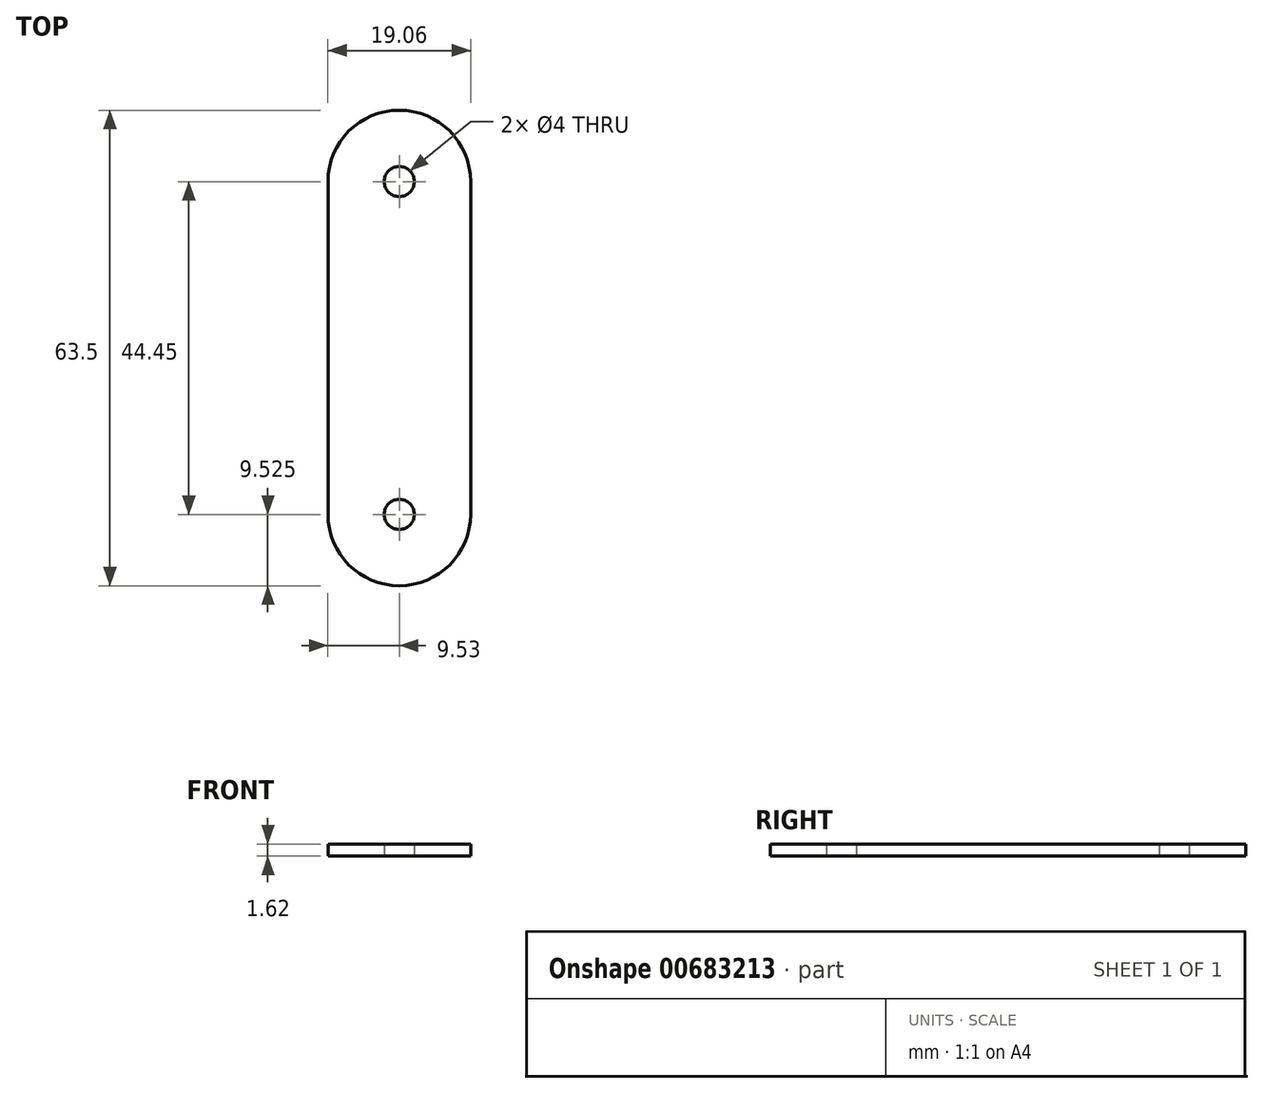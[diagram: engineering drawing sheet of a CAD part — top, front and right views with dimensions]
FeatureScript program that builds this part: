
annotation { "Feature Type Name" : "Feature", "Feature Type Description" : "" }
export const myFeature = defineFeature(function(context is Context, id is Id, definition is map)
    precondition{}
    {
        {
            var Q0;
            Q0=qCreatedBy(makeId("Top.planeOp"),FACE);
            var sketch = newSketch(context, id + "F0", { "sketchPlane" : qUnion([Q0])});
            skLineSegment(sketch, "E0.left", {"start": v(-9.52, -22.22) * mm, "end": v(-9.52, 22.23) * mm});
            skLineSegment(sketch, "E0.right", {"start": v(9.52, -22.23) * mm, "end": v(9.52, 22.23) * mm});
            skArc(sketch, "E1", {"start": v(9.52, 22.23) * mm, "mid": v(0, 31.75) * mm, "end": v(-9.53, 22.23) * mm});
            skArc(sketch, "E2", {"start": v(-9.52, -22.23) * mm, "mid": v(0, -31.75) * mm, "end": v(9.52, -22.23) * mm});
            skCircle(sketch, "E3", {"center": v(0, 22.23) * mm, "radius": 2 * mm});
            skCircle(sketch, "E4", {"center": v(0, -22.23) * mm, "radius": 2 * mm});
            skSolve(sketch);
        }
        {
            var Q0;
            Q0=makeQuery(id+"F0.imprint","IMPRINT",FACE,{"disambiguationData":[TD([[makeQuery(id+"F0.imprint","IMPRINT",EDGE,{"derivedFrom":sQuery(id+"F0.wireOp",EDGE,"E0.left")}),-1.0]])]});
            extrude(context, id + "F1", {"entities" : qUnion([Q0]), "endBound" : BoundingType.SYMMETRIC, "depth" : 1.63 * mm, "offsetDistance" : 25.4 * mm});
        }
    });
